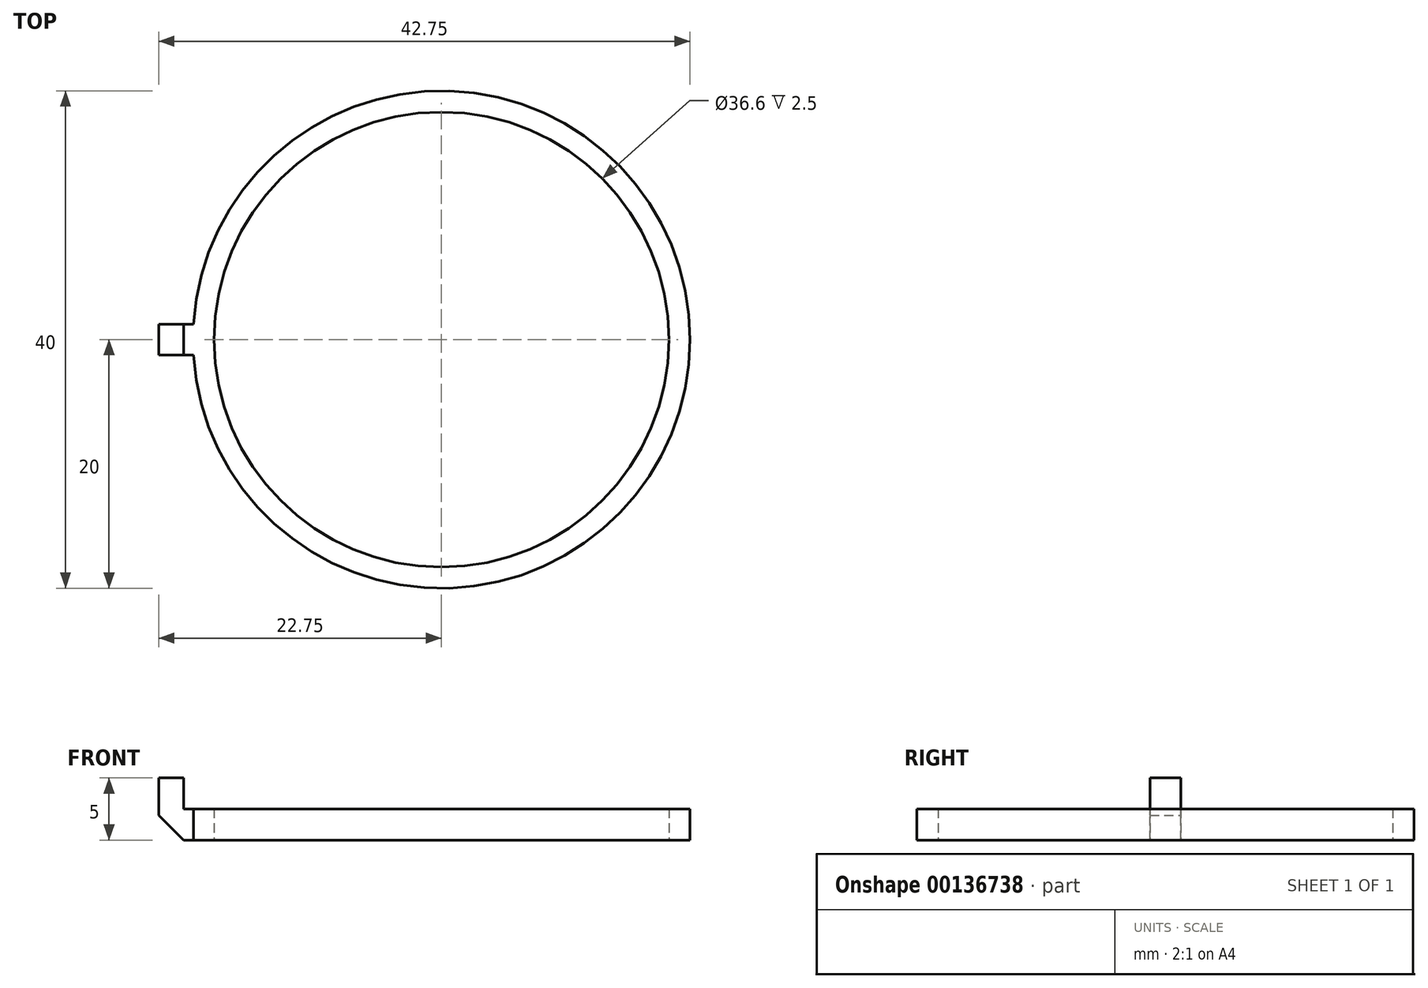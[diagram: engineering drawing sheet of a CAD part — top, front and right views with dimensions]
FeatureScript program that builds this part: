
annotation { "Feature Type Name" : "Feature", "Feature Type Description" : "" }
export const myFeature = defineFeature(function(context is Context, id is Id, definition is map)
    precondition{}
    {
        {
            var Q0;
            Q0=qCreatedBy(makeId("Top.planeOp"),FACE);
            var sketch = newSketch(context, id + "F0", { "sketchPlane" : qUnion([Q0])});
            skCircle(sketch, "E0", {"center": v(0, 0) * mm, "radius": 18.3 * mm});
            skCircle(sketch, "E1", {"center": v(0, 0) * mm, "radius": 20 * mm});
            skSolve(sketch);
        }
        {
            var Q0;
            Q0=makeQuery(id+"F0.imprint","IMPRINT",FACE,{"disambiguationData":[TD([[makeQuery(id+"F0.imprint","IMPRINT",EDGE,{"derivedFrom":sQuery(id+"F0.wireOp",EDGE,"E0")}),-1.0]])]});
            extrude(context, id + "F1", {"entities" : qUnion([Q0]), "depth" : 2.5 * mm, "offsetDistance" : 25 * mm});
        }
        {
            var Q0;
            Q0=qCreatedBy(makeId("Front.planeOp"),FACE);
            var sketch = newSketch(context, id + "F2", { "sketchPlane" : qUnion([Q0])});
            skLineSegment(sketch, "E2", {"start": v(-19.25, 0) * mm, "end": v(-20.75, 0) * mm});
            skLineSegment(sketch, "E3", {"start": v(-20.75, 0) * mm, "end": v(-22.75, 2) * mm});
            skLineSegment(sketch, "E4", {"start": v(-22.75, 2) * mm, "end": v(-22.75, 5) * mm});
            skLineSegment(sketch, "E5", {"start": v(-22.75, 5) * mm, "end": v(-20.75, 5) * mm});
            skLineSegment(sketch, "E6", {"start": v(-20.75, 5) * mm, "end": v(-20.75, 2.5) * mm});
            skLineSegment(sketch, "E7", {"start": v(-20.75, 2.5) * mm, "end": v(-19.25, 2.5) * mm});
            skLineSegment(sketch, "E8", {"start": v(-19.25, 2.5) * mm, "end": v(-19.25, 0) * mm});
            skPoint(sketch, "E9", {"position": v(-20, 0) * mm});
            skSolve(sketch);
        }
        {
            var Q0;
            Q0=makeQuery(id+"F2.imprint","IMPRINT",FACE,{"disambiguationData":[TD([[makeQuery(id+"F2.imprint","IMPRINT",EDGE,{"derivedFrom":sQuery(id+"F2.wireOp",EDGE,"E2")}),-1.0]])]});
            extrude(context, id + "F3", {"entities" : qUnion([Q0]), "operationType" : NewBodyOperationType.ADD, "endBound" : BoundingType.SYMMETRIC, "depth" : 2.5 * mm, "offsetDistance" : 25 * mm});
        }
    });
